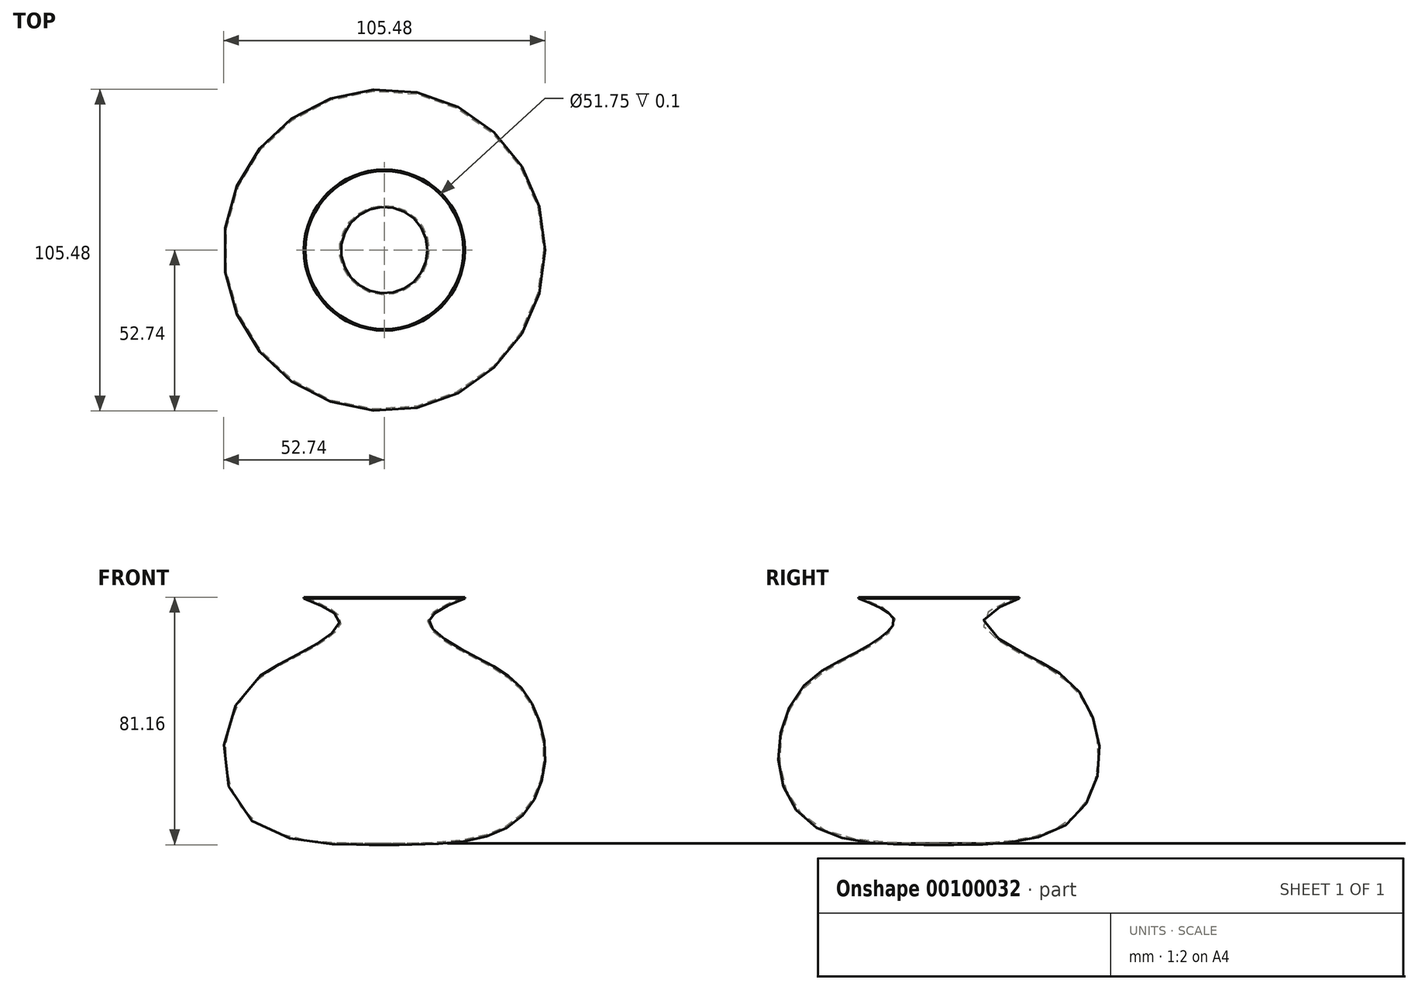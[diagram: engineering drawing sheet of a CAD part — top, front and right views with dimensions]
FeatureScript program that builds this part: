
annotation { "Feature Type Name" : "Feature", "Feature Type Description" : "" }
export const myFeature = defineFeature(function(context is Context, id is Id, definition is map)
    precondition{}
    {
        {
            var Q0;
            Q0=qCreatedBy(makeId("Front.planeOp"),FACE);
            var sketch = newSketch(context, id + "F0", { "sketchPlane" : qUnion([Q0])});
            skLineSegment(sketch, "E0", {"start": v(0, 48) * mm, "end": v(0, -32.55) * mm});
            skLineSegment(sketch, "E1", {"start": v(0, 48) * mm, "end": v(25.87, 48) * mm});
            skFitSpline(sketch, "E2", {"points": [v(25.87, 48) * mm, v(14.17, 40.35) * mm, v(25.87, 30.1) * mm, v(44.4, 18.16) * mm, v(52.2, -5.24) * mm, v(40.5, -26.7) * mm, v(0, -32.55) * mm], "startDerivative": vector(-132.67, -53.5) * mm, "endDerivative": vector(-208, 0.92) * mm});
            skSolve(sketch);
        }
        {
            var Q0;
            Q0=makeQuery(id+"F0.imprint","IMPRINT",FACE,{"disambiguationData":[TD([[makeQuery(id+"F0.imprint","IMPRINT",EDGE,{"derivedFrom":sQuery(id+"F0.wireOp",EDGE,"E0")}),1.0]])]});
            var Q1;
            Q1=sQuery(id+"F0.wireOp",EDGE,"E0");
            revolve(context, id + "F1", {"entities" : qUnion([Q0]), "axis" : qUnion([Q1]), "revolveType" : RevolveType.FULL});
        }
        {
            var Q0;
            Q0=makeQuery(id+"F1.opRevolve","SWEPT_FACE",FACE,{"disambiguationData":[OSD([sQuery(id+"F0.wireOp",EDGE,"E1")])]});
            extrude(context, id + "F2", {"entities" : qUnion([Q0]), "operationType" : NewBodyOperationType.ADD, "depth" : .1 * mm});
        }
        {
            var Q0;
            Q0=makeQuery(id+"F2.opExtrude","CAP_FACE",FACE,{"disambiguationData":[OSD([sQuery(id+"F0.wireOp",EDGE,"E1")])],"isStart":false});
            shell(context, id + "F3", {"entities" : qUnion([Q0]), "thickness" : .5 * mm, "oppositeDirection" : true});
        }
    });
